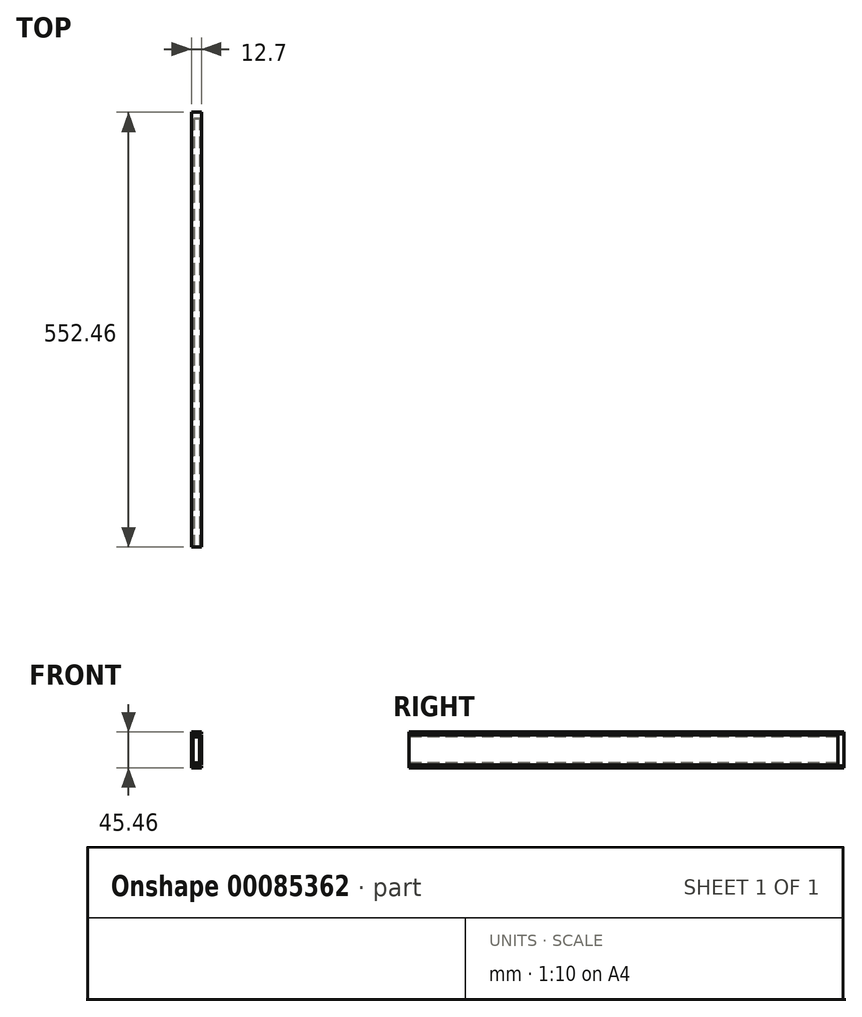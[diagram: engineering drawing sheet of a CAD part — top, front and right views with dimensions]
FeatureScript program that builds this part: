
annotation { "Feature Type Name" : "Feature", "Feature Type Description" : "" }
export const myFeature = defineFeature(function(context is Context, id is Id, definition is map)
    precondition{}
    {
        {
            var Q0;
            Q0=qCreatedBy(makeId("Front.planeOp"),FACE);
            var sketch = newSketch(context, id + "F0", { "sketchPlane" : qUnion([Q0])});
            skLineSegment(sketch, "E0", {"start": v(0, 20.45) * mm, "end": v(0, -20.45) * mm});
            skLineSegment(sketch, "E1", {"start": v(0, -20.45) * mm, "end": v(10.41, -20.45) * mm});
            skLineSegment(sketch, "E2", {"start": v(10.41, -20.45) * mm, "end": v(10.41, -22.73) * mm});
            skLineSegment(sketch, "E3", {"start": v(10.41, -22.73) * mm, "end": v(-2.29, -22.73) * mm});
            skLineSegment(sketch, "E4", {"start": v(-2.29, -22.73) * mm, "end": v(-2.29, 22.73) * mm});
            skLineSegment(sketch, "E5", {"start": v(-2.29, 22.73) * mm, "end": v(10.41, 22.73) * mm});
            skLineSegment(sketch, "E6", {"start": v(10.41, 22.73) * mm, "end": v(10.41, 20.45) * mm});
            skLineSegment(sketch, "E7", {"start": v(10.41, 20.45) * mm, "end": v(0, 20.45) * mm});
            skSolve(sketch);
        }
        {
            var Q0;
            Q0=makeQuery(id+"F0.imprint","IMPRINT",FACE,{"disambiguationData":[TD([[makeQuery(id+"F0.imprint","IMPRINT",EDGE,{"derivedFrom":sQuery(id+"F0.wireOp",EDGE,"E0")}),-1.0]])]});
            extrude(context, id + "F1", {"entities" : qUnion([Q0]), "endBound" : BoundingType.SYMMETRIC, "depth" : 552.45 * mm});
        }
        {
            var Q0;
            Q0=makeQuery(id+"F1.opExtrude","CAP_FACE",FACE,{"disambiguationData":[OSD([sQuery(id+"F0.wireOp",EDGE,"E0"),sQuery(id+"F0.wireOp",EDGE,"E1"),sQuery(id+"F0.wireOp",EDGE,"E2"),sQuery(id+"F0.wireOp",EDGE,"E3"),sQuery(id+"F0.wireOp",EDGE,"E4"),sQuery(id+"F0.wireOp",EDGE,"E5"),sQuery(id+"F0.wireOp",EDGE,"E6"),sQuery(id+"F0.wireOp",EDGE,"E7")])],"isStart":false});
            var sketch = newSketch(context, id + "F2", { "sketchPlane" : qUnion([Q0])});
            skLineSegment(sketch, "E8", {"start": v(1.27, 18.92) * mm, "end": v(1.27, 16.64) * mm});
            skLineSegment(sketch, "E9", {"start": v(1.27, 16.64) * mm, "end": v(8.13, 16.64) * mm});
            skLineSegment(sketch, "E10", {"start": v(8.13, 16.64) * mm, "end": v(8.13, -16.64) * mm});
            skLineSegment(sketch, "E11", {"start": v(8.13, -16.64) * mm, "end": v(1.27, -16.64) * mm});
            skLineSegment(sketch, "E12", {"start": v(1.27, -16.64) * mm, "end": v(1.27, -18.92) * mm});
            skLineSegment(sketch, "E13", {"start": v(1.27, -18.92) * mm, "end": v(10.41, -18.92) * mm});
            skLineSegment(sketch, "E14", {"start": v(10.41, -18.92) * mm, "end": v(10.41, 18.92) * mm});
            skLineSegment(sketch, "E15", {"start": v(10.41, 18.92) * mm, "end": v(1.27, 18.92) * mm});
            skSolve(sketch);
        }
        {
            var Q0;
            Q0=makeQuery(id+"F2.imprint","IMPRINT",FACE,{"disambiguationData":[TD([[makeQuery(id+"F2.imprint","IMPRINT",EDGE,{"derivedFrom":sQuery(id+"F2.wireOp",EDGE,"E8")}),1.0]])]});
            extrude(context, id + "F3", {"entities" : qUnion([Q0]), "oppositeDirection" : true, "depth" : 544.5 * mm});
        }
        {
            var Q0;
            Q0=makeQuery(id+"F1.opExtrude","CAP_FACE",FACE,{"disambiguationData":[OSD([sQuery(id+"F0.wireOp",EDGE,"E0"),sQuery(id+"F0.wireOp",EDGE,"E1"),sQuery(id+"F0.wireOp",EDGE,"E2"),sQuery(id+"F0.wireOp",EDGE,"E3"),sQuery(id+"F0.wireOp",EDGE,"E4"),sQuery(id+"F0.wireOp",EDGE,"E5"),sQuery(id+"F0.wireOp",EDGE,"E6"),sQuery(id+"F0.wireOp",EDGE,"E7")])],"isStart":true});
            var sketch = newSketch(context, id + "F4", { "sketchPlane" : qUnion([Q0])});
            skPoint(sketch, "E16", {"position": v(0, 0) * mm});
            skSolve(sketch);
        }
    });
